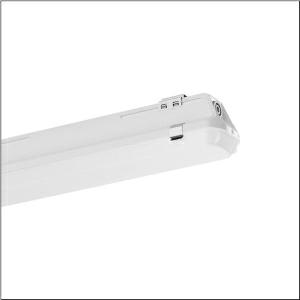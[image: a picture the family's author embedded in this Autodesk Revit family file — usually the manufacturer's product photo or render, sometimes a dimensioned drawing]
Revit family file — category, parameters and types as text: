
# Revit family: monsun_r__21_51fb10dp360b_a0ac
name_source: partatom
category: Lighting Fixtures
units: mm (PartAtom-declared; Revit-internal decimal feet)

## family parameters
Cut with Voids When Loaded = No
Host = Face
Light Source = No
Part Type = Normal
Room Calculation Point = No
Round Connector Dimension = Use Diameter
Shared = No

## types (1)
- --- (1 x LED, 6060 lm, 43.2 W, 3000K)
    Apparent Load = 43 VA
    CIE Flux Codes = 47 77 93 94 100
    Color Rendering = 80
    Color Temperature = 3000K
    Default Elevation = 1800 mm
    Description = Monsun® 21, damp-proof luminaire, chain hanger, primary optical cover: enclosure, of PMMA, light emission: direct distribution, primary light characteristic: symmetric, installation type: suspended mounting, surface-mounted, horizontal mounting, vertical mounting, LED, rated luminous flux: 6.060lm, luminous efficacy: 154lm/W, light colour: 830, colour temperature: 3000K, control gear: ECG DALI, with terminal, 5-pole, max. 2.5mm², mains connection: 220..240V, AC, 50/60Hz, rated input power: 39W, housing, of glass-fibre reinforced polyester, uncoated, bright grey, incl. chain hanger, length: 1.590mm, width: 90mm, height: 88mm, clip for enclosure, of stainless steel (V2A), ceiling mounting element, of stainless steel (V2A), chain hanger, of stainless steel (V2A), protection rating (complete): IP66, insulation class (complete): insulation class I (protective earthing), certification: CE, ENEC, VDE, UKCA, protection symbol: D, impact resistance: IK04, permissible operating ambient temperature: -25..+35°C, standard: EN 50419, EN 60598-2-1, corresponds to IFS (International Featured Standards) requirements for safety and quality in the food industry, for indoor or canopied outdoor use, no direct snow, no direct sun, no direct rain, contact your sales advisor before using the luminaires in applications with unclear chemical exposure, large temperature fluctuations or condensation-forming humidity, LABS conformity tested according to VDMA 24364:2018-05, packaging unit: 1 piece
    Height = 89 mm
    Lamp = 1 x LED
    Lamp Light Flux = 6060 lm
    Lamp Power = 43.2 W
    Lamp count = 1
    Length = 1590 mm
    Luminous efficacy = 140 lm/W
    Manufacturer = Siteco
    ModVariant = No
    Model = 51FB10DP360B
    Mounting Place = Ceiling
    Mounting Type = Surface mounted
    Number of Poles = 1
    OnlyDefault = Yes
    Power Factor = 1
    Product Name = Monsun® 21
    Product group = damp-proof luminaire
    ProductGroupID = 300
    Protection Class = Protection class I
    Protection Degree = IP 66
    RLX_Detail_Level = 1
    RLX_Emergency_Light_Flux = 0 lm
    RLX_Emergency_Type = 0
    RLX_Emergency_Type_DB = No
    RlxData = <blob elided: 92273 chars, md5=cd5949e2>
    Socket = socket
    Standby Power = 0 W
    System Light Flux = 6060 lm
    System Power = 43 W
    Type Comments = factory setting: luminous flux: 100 % | dim-lin: 254 | 286 mA
    Type Image = l_1319656.jpg
    URL = http://relux.com
    VarID = @adj_116857
    Voltage = 0 V
    Weight = 0.00 kg
    Width = 90 mm

## geometry (parser evidence)
native form markers: Blend x4, Sweep x13
no freeform markers — native parametric forms only
